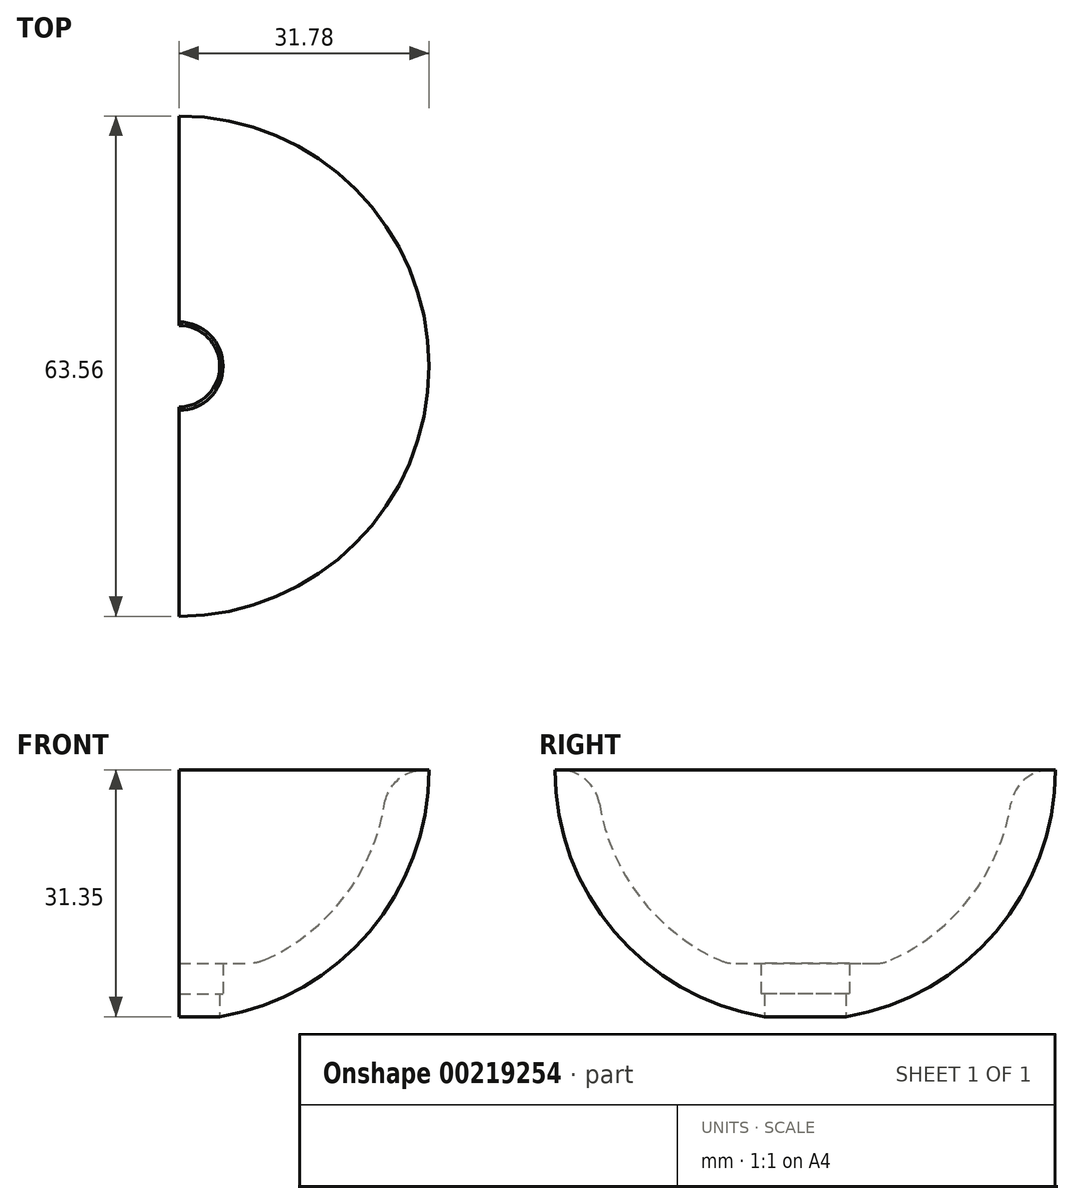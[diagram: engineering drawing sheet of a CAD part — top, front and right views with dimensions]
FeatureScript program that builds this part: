
annotation { "Feature Type Name" : "Feature", "Feature Type Description" : "" }
export const myFeature = defineFeature(function(context is Context, id is Id, definition is map)
    precondition{}
    {
        {
            var Q0;
            Q0=qCreatedBy(makeId("Front.planeOp"),FACE);
            var sketch = newSketch(context, id + "F0", { "sketchPlane" : qUnion([Q0])});
            skArc(sketch, "E0", {"start": v(-31.78, 0) * mm, "mid": v(-24.24, -20.55) * mm, "end": v(-5.2, -31.35) * mm});
            skLineSegment(sketch, "E1", {"start": v(-31.78, 0) * mm, "end": v(-26.5, 0) * mm});
            skLineSegment(sketch, "E2", {"start": v(-26.5, 0) * mm, "end": v(-31.78, 0) * mm});
            skLineSegment(sketch, "E3", {"start": v(-5.2, -31.35) * mm, "end": v(-5.2, -28.48) * mm});
            skLineSegment(sketch, "E4", {"start": v(-5.2, -28.48) * mm, "end": v(-5.61, -28.48) * mm});
            skLineSegment(sketch, "E5", {"start": v(-5.61, -28.48) * mm, "end": v(-5.61, -24.6) * mm});
            skLineSegment(sketch, "E6", {"start": v(-9.85, -24.6) * mm, "end": v(-5.61, -24.6) * mm});
            skArc(sketch, "E7", {"start": v(-26.5, 0) * mm, "mid": v(-21.95, -14.85) * mm, "end": v(-9.85, -24.6) * mm});
            skLineSegment(sketch, "E8", {"start": v(0, -32.66) * mm, "end": v(0, -24.21) * mm});
            skSolve(sketch);
        }
        {
            var Q0;
            Q0=makeQuery(id+"F0.imprint","IMPRINT",FACE,{"disambiguationData":[TD([[makeQuery(id+"F0.imprint","IMPRINT",EDGE,{"derivedFrom":sQuery(id+"F0.wireOp",EDGE,"E0")}),1.0]])]});
            var Q1;
            Q1=sQuery(id+"F0.wireOp",EDGE,"E8");
            revolve(context, id + "F1", {"entities" : qUnion([Q0]), "axis" : qUnion([Q1]), "revolveType" : RevolveType.FULL});
        }
        {
            var Q0;
            Q0=makeQuery(id+"F1.opRevolve","SWEPT_EDGE",EDGE,{"disambiguationData":[OSD([sQuery(id+"F0.wireOp",EDGE,"E2"),sQuery(id+"F0.wireOp",EDGE,"E7")])]});
            fillet(context, id + "F2", {"entities" : qUnion([Q0]), "radius" : 5.08 * mm, "tangentPropagation" : true, "allowEdgeOverflow" : false});
        }
        {
            var Q0;
            Q0=qCreatedBy(makeId("Right.planeOp"),FACE);
            var sketch = newSketch(context, id + "F3", { "sketchPlane" : qUnion([Q0])});
            skLineSegment(sketch, "E9.bottom", {"start": v(36.96, 0) * mm, "end": v(-38.26, 0) * mm});
            skLineSegment(sketch, "E9.top", {"start": v(36.96, -48.3) * mm, "end": v(-38.26, -48.3) * mm});
            skLineSegment(sketch, "E9.left", {"start": v(36.96, 0) * mm, "end": v(36.96, -48.3) * mm});
            skLineSegment(sketch, "E9.right", {"start": v(-38.26, 0) * mm, "end": v(-38.26, -48.3) * mm});
            skSolve(sketch);
        }
        {
            var Q0;
            Q0=makeQuery(id+"F3.imprint","IMPRINT",FACE,{"disambiguationData":[TD([[makeQuery(id+"F3.imprint","IMPRINT",EDGE,{"derivedFrom":sQuery(id+"F3.wireOp",EDGE,"E9.bottom")}),1.0]])]});
            extrude(context, id + "F4", {"entities" : qUnion([Q0]), "operationType" : NewBodyOperationType.REMOVE, "oppositeDirection" : true, "depth" : 34.3 * mm});
        }
    });
